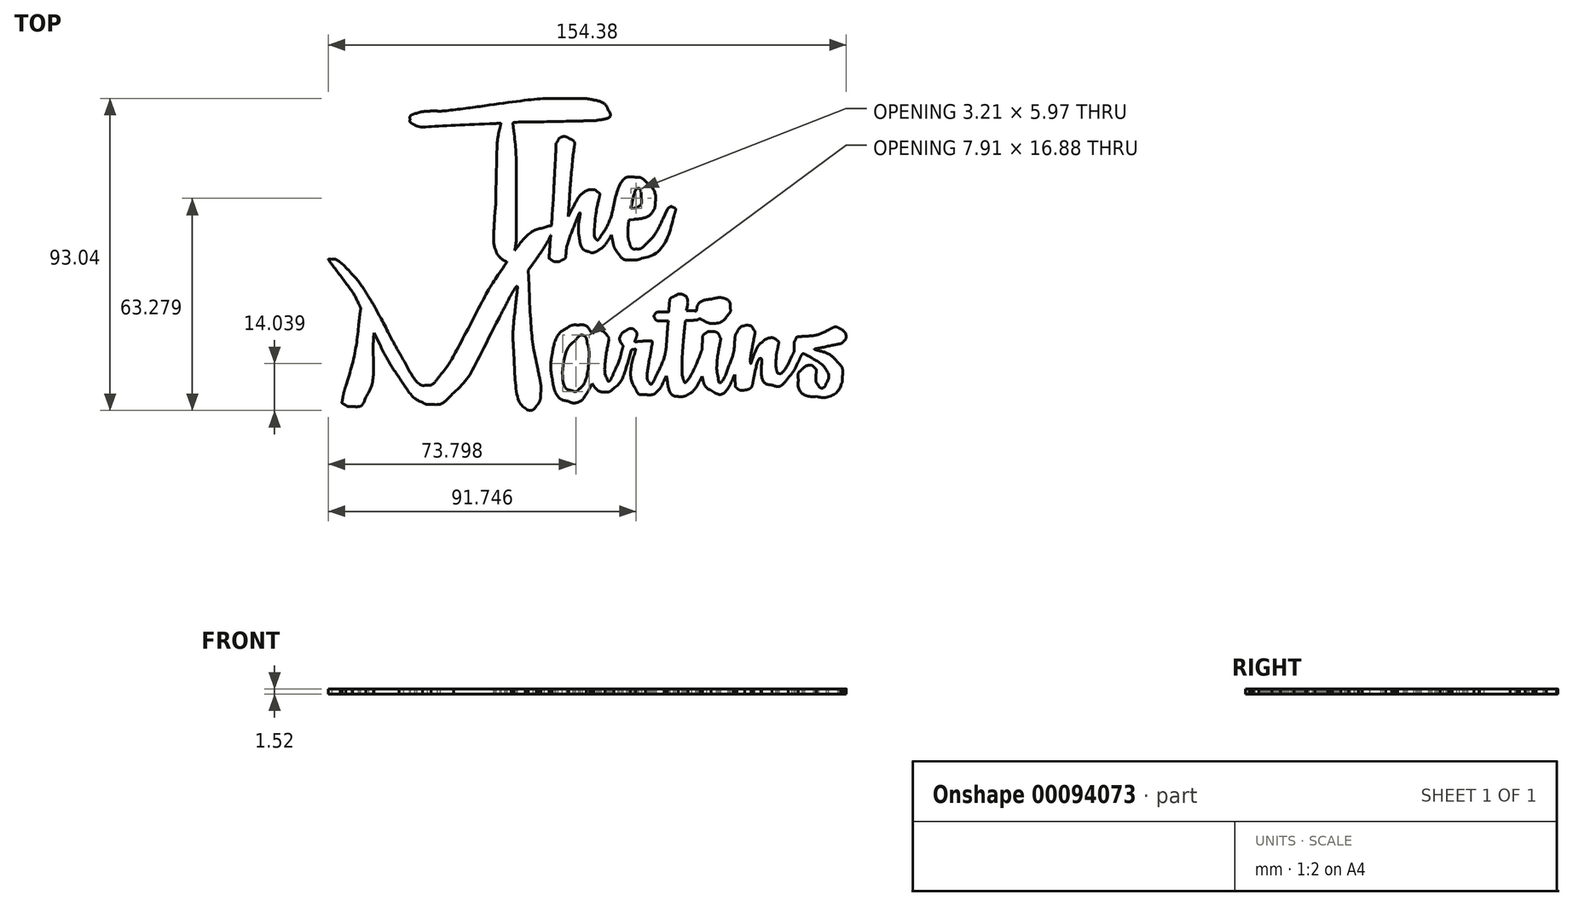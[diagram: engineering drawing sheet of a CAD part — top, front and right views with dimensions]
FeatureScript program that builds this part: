
annotation { "Feature Type Name" : "Feature", "Feature Type Description" : "" }
export const myFeature = defineFeature(function(context is Context, id is Id, definition is map)
    precondition{}
    {
        {
            var Q0;
            Q0=qCreatedBy(makeId("Top.planeOp"),FACE);
            var sketch = newSketch(context, id + "F0", { "sketchPlane" : qUnion([Q0])});
            skLineSegment(sketch, "E0", {"start": v(-54.49, 3450.18) * mm, "end": v(-56.26, 3453.65) * mm});
            skLineSegment(sketch, "E1", {"start": v(-56.26, 3453.65) * mm, "end": v(-56.34, 3452) * mm});
            skLineSegment(sketch, "E2", {"start": v(-56.34, 3452) * mm, "end": v(-54.49, 3450.18) * mm});
            skLineSegment(sketch, "E3", {"start": v(-8.87, 3474.22) * mm, "end": v(-10.27, 3472.28) * mm});
            skLineSegment(sketch, "E4", {"start": v(-10.27, 3472.28) * mm, "end": v(-10.04, 3467.72) * mm});
            skLineSegment(sketch, "E5", {"start": v(-10.04, 3467.72) * mm, "end": v(-8.87, 3474.22) * mm});
            skLineSegment(sketch, "E6", {"start": v(8.5, 3453.96) * mm, "end": v(8.88, 3453.46) * mm});
            skLineSegment(sketch, "E7", {"start": v(8.88, 3453.46) * mm, "end": v(9.39, 3453.76) * mm});
            skLineSegment(sketch, "E8", {"start": v(9.39, 3453.76) * mm, "end": v(8.5, 3453.96) * mm});
            skLineSegment(sketch, "E9", {"start": v(31.4, 3456.4) * mm, "end": v(31.5, 3457.23) * mm});
            skLineSegment(sketch, "E10", {"start": v(31.5, 3457.23) * mm, "end": v(30.1, 3457.23) * mm});
            skLineSegment(sketch, "E11", {"start": v(30.1, 3457.23) * mm, "end": v(31.4, 3456.4) * mm});
            skLineSegment(sketch, "E12", {"start": v(37.13, 3461.41) * mm, "end": v(36.9, 3460.24) * mm});
            skLineSegment(sketch, "E13", {"start": v(36.9, 3460.24) * mm, "end": v(38.12, 3460.24) * mm});
            skLineSegment(sketch, "E14", {"start": v(38.12, 3460.24) * mm, "end": v(37.13, 3461.41) * mm});
            skLineSegment(sketch, "E15", {"start": v(38.35, 3457.4) * mm, "end": v(36.61, 3457.31) * mm});
            skLineSegment(sketch, "E16", {"start": v(36.61, 3457.31) * mm, "end": v(36.43, 3455.5) * mm});
            skLineSegment(sketch, "E17", {"start": v(36.43, 3455.5) * mm, "end": v(38.35, 3457.4) * mm});
            skLineSegment(sketch, "E18", {"start": v(51.4, 3439.4) * mm, "end": v(51.32, 3441.18) * mm});
            skLineSegment(sketch, "E19", {"start": v(51.32, 3441.18) * mm, "end": v(50.86, 3440.31) * mm});
            skLineSegment(sketch, "E20", {"start": v(50.86, 3440.31) * mm, "end": v(51.4, 3439.4) * mm});
            skLineSegment(sketch, "E21", {"start": v(41.74, 3440.04) * mm, "end": v(41.56, 3440.76) * mm});
            skLineSegment(sketch, "E22", {"start": v(41.56, 3440.76) * mm, "end": v(41.03, 3439.73) * mm});
            skLineSegment(sketch, "E23", {"start": v(41.03, 3439.73) * mm, "end": v(41.74, 3440.04) * mm});
            skLineSegment(sketch, "E24", {"start": v(31.16, 3439.74) * mm, "end": v(30.96, 3440.82) * mm});
            skLineSegment(sketch, "E25", {"start": v(30.96, 3440.82) * mm, "end": v(30.45, 3439.87) * mm});
            skLineSegment(sketch, "E26", {"start": v(30.45, 3439.87) * mm, "end": v(31.16, 3439.74) * mm});
            skLineSegment(sketch, "E27", {"start": v(9.34, 3437.83) * mm, "end": v(8.78, 3438.57) * mm});
            skLineSegment(sketch, "E28", {"start": v(8.78, 3438.57) * mm, "end": v(8.19, 3437.35) * mm});
            skLineSegment(sketch, "E29", {"start": v(8.19, 3437.35) * mm, "end": v(9.34, 3437.83) * mm});
            skLineSegment(sketch, "E30", {"start": v(1.75, 3489.42) * mm, "end": v(1.66, 3488.4) * mm});
            skLineSegment(sketch, "E31", {"start": v(1.66, 3488.4) * mm, "end": v(2.42, 3489.81) * mm});
            skLineSegment(sketch, "E32", {"start": v(2.42, 3489.81) * mm, "end": v(1.75, 3489.42) * mm});
            skLineSegment(sketch, "E33", {"start": v(21.22, 3487.5) * mm, "end": v(19.72, 3487.31) * mm});
            skLineSegment(sketch, "E34", {"start": v(19.72, 3487.31) * mm, "end": v(19.6, 3485.98) * mm});
            skLineSegment(sketch, "E35", {"start": v(19.6, 3485.98) * mm, "end": v(21.22, 3487.5) * mm});
            skLineSegment(sketch, "E36", {"start": v(14.8, 3481.58) * mm, "end": v(14.54, 3482.83) * mm});
            skLineSegment(sketch, "E37", {"start": v(14.54, 3482.83) * mm, "end": v(14.13, 3482.13) * mm});
            skLineSegment(sketch, "E38", {"start": v(14.13, 3482.13) * mm, "end": v(14.8, 3481.58) * mm});
            skLineSegment(sketch, "E39", {"start": v(-3.19, 3475.34) * mm, "end": v(-3.19, 3475.34) * mm});
            skLineSegment(sketch, "E40", {"start": v(20.42, 3491.25) * mm, "end": v(20.3, 3490.8) * mm});
            skLineSegment(sketch, "E41", {"start": v(20.3, 3490.8) * mm, "end": v(21.22, 3490.9) * mm});
            skLineSegment(sketch, "E42", {"start": v(21.22, 3490.9) * mm, "end": v(20.42, 3491.25) * mm});
            skFitSpline(sketch, "E43", {"points": [v(-10.23, 3430.63) * mm, v(-10.43, 3430.66) * mm, v(-10.81, 3430.92) * mm, v(-11.1, 3431.2) * mm]});
            skFitSpline(sketch, "E44", {"points": [v(-11.1, 3431.2) * mm, v(-12.81, 3432.91) * mm, v(-14.07, 3438.99) * mm, v(-14.56, 3447.98) * mm]});
            skFitSpline(sketch, "E45", {"points": [v(-14.56, 3447.98) * mm, v(-14.79, 3452.08) * mm, v(-14.67, 3455.56) * mm, v(-14.17, 3460.4) * mm]});
            skFitSpline(sketch, "E46", {"points": [v(-14.17, 3460.4) * mm, v(-13.75, 3464.32) * mm, v(-13.52, 3467.51) * mm, v(-13.64, 3467.51) * mm]});
            skFitSpline(sketch, "E47", {"points": [v(-13.64, 3467.51) * mm, v(-13.72, 3467.51) * mm, v(-14.71, 3466.04) * mm, v(-15.38, 3464.91) * mm]});
            skFitSpline(sketch, "E48", {"points": [v(-15.38, 3464.91) * mm, v(-15.64, 3464.47) * mm, v(-17.24, 3461.4) * mm, v(-18.93, 3458.1) * mm]});
            skFitSpline(sketch, "E49", {"points": [v(-18.93, 3458.1) * mm, v(-26.38, 3443.57) * mm, v(-28.95, 3439.34) * mm, v(-32.5, 3435.8) * mm]});
            skFitSpline(sketch, "E50", {"points": [v(-32.5, 3435.8) * mm, v(-35.08, 3433.23) * mm, v(-36.76, 3432.36) * mm, v(-39.15, 3432.34) * mm]});
            skFitSpline(sketch, "E51", {"points": [v(-39.15, 3432.34) * mm, v(-40.51, 3432.33) * mm, v(-40.65, 3432.36) * mm, v(-41.78, 3432.93) * mm]});
            skFitSpline(sketch, "E52", {"points": [v(-41.78, 3432.93) * mm, v(-43.95, 3434.03) * mm, v(-45.66, 3435.87) * mm, v(-48.73, 3440.4) * mm]});
            skFitSpline(sketch, "E53", {"points": [v(-48.73, 3440.4) * mm, v(-50.96, 3443.68) * mm, v(-52.51, 3446.32) * mm, v(-54.49, 3450.18) * mm]});
            skFitSpline(sketch, "E54", {"points": [v(-56.34, 3452) * mm, v(-56.4, 3451.1) * mm, v(-56.43, 3448.86) * mm, v(-56.42, 3447.04) * mm]});
            skFitSpline(sketch, "E55", {"points": [v(-56.42, 3447.04) * mm, v(-56.4, 3441.12) * mm, v(-57, 3437.63) * mm, v(-58.57, 3434.48) * mm]});
            skFitSpline(sketch, "E56", {"points": [v(-58.57, 3434.48) * mm, v(-59.68, 3432.28) * mm, v(-60.52, 3431.7) * mm, v(-62.62, 3431.7) * mm]});
            skFitSpline(sketch, "E57", {"points": [v(-62.62, 3431.7) * mm, v(-63.74, 3431.7) * mm, v(-64.07, 3431.76) * mm, v(-64.62, 3432.07) * mm]});
            skFitSpline(sketch, "E58", {"points": [v(-64.62, 3432.07) * mm, v(-65.6, 3432.63) * mm, v(-65.7, 3432.94) * mm, v(-65.47, 3434.41) * mm]});
            skFitSpline(sketch, "E59", {"points": [v(-65.47, 3434.41) * mm, v(-65.36, 3435.09) * mm, v(-64.98, 3436.6) * mm, v(-64.63, 3437.78) * mm]});
            skFitSpline(sketch, "E60", {"points": [v(-64.63, 3437.78) * mm, v(-62.74, 3444.11) * mm, v(-61.4, 3450.5) * mm, v(-60.73, 3456.42) * mm]});
            skFitSpline(sketch, "E61", {"points": [v(-60.73, 3456.42) * mm, v(-60.56, 3457.87) * mm, v(-60.38, 3459.37) * mm, v(-60.33, 3459.77) * mm]});
            skFitSpline(sketch, "E62", {"points": [v(-60.33, 3459.77) * mm, v(-60.17, 3461.02) * mm, v(-60.2, 3461.18) * mm, v(-60.95, 3462.73) * mm]});
            skFitSpline(sketch, "E63", {"points": [v(-60.95, 3462.73) * mm, v(-61.92, 3464.74) * mm, v(-63.23, 3466.73) * mm, v(-66.27, 3470.77) * mm]});
            skFitSpline(sketch, "E64", {"points": [v(-66.27, 3470.77) * mm, v(-69.72, 3475.38) * mm, v(-69.82, 3475.58) * mm, v(-68.73, 3475.58) * mm]});
            skFitSpline(sketch, "E65", {"points": [v(-68.73, 3475.58) * mm, v(-67.74, 3475.58) * mm, v(-65.03, 3473.61) * mm, v(-63.01, 3471.44) * mm]});
            skFitSpline(sketch, "E66", {"points": [v(-63.01, 3471.44) * mm, v(-61.56, 3469.86) * mm, v(-59.31, 3466.84) * mm, v(-57.85, 3464.48) * mm]});
            skFitSpline(sketch, "E67", {"points": [v(-57.85, 3464.48) * mm, v(-56.4, 3462.14) * mm, v(-54.94, 3459.5) * mm, v(-51.63, 3453.21) * mm]});
            skFitSpline(sketch, "E68", {"points": [v(-51.63, 3453.21) * mm, v(-50.26, 3450.61) * mm, v(-48.98, 3448.23) * mm, v(-48.79, 3447.92) * mm]});
            skFitSpline(sketch, "E69", {"points": [v(-48.79, 3447.92) * mm, v(-48.59, 3447.6) * mm, v(-47.96, 3446.53) * mm, v(-47.4, 3445.52) * mm]});
            skFitSpline(sketch, "E70", {"points": [v(-47.4, 3445.52) * mm, v(-44.77, 3440.86) * mm, v(-42.17, 3438.12) * mm, v(-40.37, 3438.1) * mm]});
            skFitSpline(sketch, "E71", {"points": [v(-40.37, 3438.1) * mm, v(-39.2, 3438.1) * mm, v(-38.13, 3438.9) * mm, v(-36.5, 3441) * mm]});
            skFitSpline(sketch, "E72", {"points": [v(-36.5, 3441) * mm, v(-34.1, 3444.1) * mm, v(-32.06, 3447.55) * mm, v(-27.14, 3456.87) * mm]});
            skFitSpline(sketch, "E73", {"points": [v(-27.14, 3456.87) * mm, v(-22.54, 3465.6) * mm, v(-20.6, 3468.94) * mm, v(-17.3, 3473.68) * mm]});
            skFitSpline(sketch, "E74", {"points": [v(-17.3, 3473.68) * mm, v(-12.76, 3480.23) * mm, v(-8.86, 3484) * mm, v(-5.58, 3485) * mm]});
            skFitSpline(sketch, "E75", {"points": [v(-5.58, 3485) * mm, v(-3.72, 3485.56) * mm, v(-2.98, 3485.12) * mm, v(-3.3, 3483.65) * mm]});
            skFitSpline(sketch, "E76", {"points": [v(-3.3, 3483.65) * mm, v(-3.4, 3483.2) * mm, v(-3.66, 3482.48) * mm, v(-3.89, 3482.03) * mm]});
            skFitSpline(sketch, "E77", {"points": [v(-3.89, 3482.03) * mm, v(-4.58, 3480.66) * mm, v(-7.39, 3476.26) * mm, v(-8.87, 3474.22) * mm]});
            skFitSpline(sketch, "E78", {"points": [v(-10.04, 3467.72) * mm, v(-9.45, 3456.35) * mm, v(-8.8, 3450.07) * mm, v(-7.6, 3443.95) * mm]});
            skFitSpline(sketch, "E79", {"points": [v(-7.6, 3443.95) * mm, v(-6.62, 3439.05) * mm, v(-6.42, 3437.56) * mm, v(-6.5, 3435.7) * mm]});
            skFitSpline(sketch, "E80", {"points": [v(-6.5, 3435.7) * mm, v(-6.58, 3434.13) * mm, v(-6.98, 3432.94) * mm, v(-7.84, 3431.82) * mm]});
            skFitSpline(sketch, "E81", {"points": [v(-7.84, 3431.82) * mm, v(-8.49, 3430.97) * mm, v(-9.42, 3430.5) * mm, v(-10.23, 3430.63) * mm]});
            skFitSpline(sketch, "E82", {"points": [v(1.65, 3433.3) * mm, v(-0.63, 3433.99) * mm, v(-2.37, 3436.52) * mm, v(-3.08, 3440.16) * mm]});
            skFitSpline(sketch, "E83", {"points": [v(-3.08, 3440.16) * mm, v(-3.41, 3441.9) * mm, v(-3.42, 3445.47) * mm, v(-3.08, 3447.21) * mm]});
            skFitSpline(sketch, "E84", {"points": [v(-3.08, 3447.21) * mm, v(-2.4, 3450.82) * mm, v(-0.8, 3453.68) * mm, v(1.3, 3455.06) * mm]});
            skFitSpline(sketch, "E85", {"points": [v(1.3, 3455.06) * mm, v(2.44, 3455.8) * mm, v(3.15, 3456) * mm, v(4.6, 3456) * mm]});
            skFitSpline(sketch, "E86", {"points": [v(4.6, 3456) * mm, v(6.4, 3456) * mm, v(7.3, 3455.52) * mm, v(8.5, 3453.96) * mm]});
            skFitSpline(sketch, "E87", {"points": [v(9.39, 3453.76) * mm, v(10.43, 3454.4) * mm, v(12.3, 3454.01) * mm, v(13.18, 3452.98) * mm]});
            skFitSpline(sketch, "E88", {"points": [v(13.18, 3452.98) * mm, v(13.78, 3452.26) * mm, v(13.83, 3451.9) * mm, v(13.55, 3450.32) * mm]});
            skFitSpline(sketch, "E89", {"points": [v(13.55, 3450.32) * mm, v(12.85, 3446.4) * mm, v(12.66, 3441.4) * mm, v(13.16, 3440.28) * mm]});
            skFitSpline(sketch, "E90", {"points": [v(13.16, 3440.28) * mm, v(13.65, 3439.2) * mm, v(14.22, 3439.61) * mm, v(15.28, 3441.82) * mm]});
            skFitSpline(sketch, "E91", {"points": [v(15.28, 3441.82) * mm, v(16.01, 3443.36) * mm, v(17.3, 3446.76) * mm, v(17.47, 3447.61) * mm]});
            skFitSpline(sketch, "E92", {"points": [v(17.47, 3447.61) * mm, v(17.53, 3447.9) * mm, v(17.69, 3448.49) * mm, v(17.82, 3448.91) * mm]});
            skFitSpline(sketch, "E93", {"points": [v(17.82, 3448.91) * mm, v(18.06, 3449.65) * mm, v(18.05, 3449.7) * mm, v(17.72, 3450.31) * mm]});
            skFitSpline(sketch, "E94", {"points": [v(17.72, 3450.31) * mm, v(17, 3451.57) * mm, v(17.58, 3453.4) * mm, v(18.97, 3454.35) * mm]});
            skFitSpline(sketch, "E95", {"points": [v(18.97, 3454.35) * mm, v(19.74, 3454.87) * mm, v(21.06, 3454.85) * mm, v(21.6, 3454.32) * mm]});
            skFitSpline(sketch, "E96", {"points": [v(21.6, 3454.32) * mm, v(22.05, 3453.86) * mm, v(22.11, 3452.81) * mm, v(21.74, 3451.78) * mm]});
            skFitSpline(sketch, "E97", {"points": [v(21.74, 3451.78) * mm, v(21.62, 3451.43) * mm, v(21.51, 3451.12) * mm, v(21.51, 3451.08) * mm]});
            skFitSpline(sketch, "E98", {"points": [v(21.51, 3451.08) * mm, v(21.51, 3451.05) * mm, v(22.37, 3451.07) * mm, v(23.41, 3451.13) * mm]});
            skFitSpline(sketch, "E99", {"points": [v(23.41, 3451.13) * mm, v(26.28, 3451.3) * mm, v(26.73, 3451.06) * mm, v(26.53, 3449.44) * mm]});
            skFitSpline(sketch, "E100", {"points": [v(26.53, 3449.44) * mm, v(26.48, 3449.07) * mm, v(26.25, 3447.74) * mm, v(26.02, 3446.48) * mm]});
            skFitSpline(sketch, "E101", {"points": [v(26.02, 3446.48) * mm, v(25.46, 3443.48) * mm, v(25.3, 3439.73) * mm, v(25.68, 3439.13) * mm]});
            skFitSpline(sketch, "E102", {"points": [v(25.68, 3439.13) * mm, v(26.22, 3438.3) * mm, v(26.83, 3438.77) * mm, v(27.84, 3440.79) * mm]});
            skFitSpline(sketch, "E103", {"points": [v(27.84, 3440.79) * mm, v(28.98, 3443.07) * mm, v(30.32, 3446.5) * mm, v(30.65, 3447.98) * mm]});
            skFitSpline(sketch, "E104", {"points": [v(30.65, 3447.98) * mm, v(30.75, 3448.42) * mm, v(30.94, 3450.3) * mm, v(31.07, 3452.17) * mm]});
            skFitSpline(sketch, "E105", {"points": [v(31.07, 3452.17) * mm, v(31.2, 3454.04) * mm, v(31.36, 3455.95) * mm, v(31.4, 3456.4) * mm]});
            skFitSpline(sketch, "E106", {"points": [v(30.1, 3457.23) * mm, v(28.51, 3457.23) * mm, v(27.74, 3457.52) * mm, v(27.39, 3458.25) * mm]});
            skFitSpline(sketch, "E107", {"points": [v(27.39, 3458.25) * mm, v(27.2, 3458.62) * mm, v(27.21, 3458.73) * mm, v(27.44, 3459.08) * mm]});
            skFitSpline(sketch, "E108", {"points": [v(27.44, 3459.08) * mm, v(27.84, 3459.7) * mm, v(28.6, 3459.92) * mm, v(30.2, 3459.92) * mm]});
            skFitSpline(sketch, "E109", {"points": [v(30.2, 3459.92) * mm, v(31.24, 3459.92) * mm, v(31.63, 3459.98) * mm, v(31.63, 3460.12) * mm]});
            skFitSpline(sketch, "E110", {"points": [v(31.63, 3460.12) * mm, v(31.64, 3460.23) * mm, v(31.7, 3460.98) * mm, v(31.78, 3461.78) * mm]});
            skFitSpline(sketch, "E111", {"points": [v(31.78, 3461.78) * mm, v(31.95, 3463.48) * mm, v(32.26, 3464.06) * mm, v(33.28, 3464.52) * mm]});
            skFitSpline(sketch, "E112", {"points": [v(33.28, 3464.52) * mm, v(34.85, 3465.24) * mm, v(36.9, 3464.44) * mm, v(37.27, 3462.97) * mm]});
            skFitSpline(sketch, "E113", {"points": [v(37.27, 3462.97) * mm, v(37.32, 3462.76) * mm, v(37.26, 3462.06) * mm, v(37.13, 3461.41) * mm]});
            skFitSpline(sketch, "E114", {"points": [v(38.12, 3460.24) * mm, v(38.8, 3460.24) * mm, v(39.46, 3460.2) * mm, v(39.58, 3460.15) * mm]});
            skFitSpline(sketch, "E115", {"points": [v(39.58, 3460.15) * mm, v(39.75, 3460.09) * mm, v(39.86, 3460.25) * mm, v(39.98, 3460.74) * mm]});
            skFitSpline(sketch, "E116", {"points": [v(39.98, 3460.74) * mm, v(40.34, 3462.16) * mm, v(42.17, 3463.38) * mm, v(44.43, 3463.73) * mm]});
            skFitSpline(sketch, "E117", {"points": [v(44.43, 3463.73) * mm, v(47.26, 3464.16) * mm, v(49.63, 3463.1) * mm, v(49.9, 3461.25) * mm]});
            skFitSpline(sketch, "E118", {"points": [v(49.9, 3461.25) * mm, v(50.05, 3460.28) * mm, v(49.87, 3459.72) * mm, v(49.16, 3458.9) * mm]});
            skFitSpline(sketch, "E119", {"points": [v(49.16, 3458.9) * mm, v(47.58, 3457.1) * mm, v(44.1, 3456.49) * mm, v(41.6, 3457.56) * mm]});
            skFitSpline(sketch, "E120", {"points": [v(41.6, 3457.56) * mm, v(40.93, 3457.85) * mm, v(40.78, 3457.87) * mm, v(40.46, 3457.68) * mm]});
            skFitSpline(sketch, "E121", {"points": [v(40.46, 3457.68) * mm, v(40.24, 3457.56) * mm, v(39.37, 3457.44) * mm, v(38.35, 3457.4) * mm]});
            skFitSpline(sketch, "E122", {"points": [v(36.43, 3455.5) * mm, v(35.85, 3449.64) * mm, v(35.63, 3441.23) * mm, v(36.03, 3439.87) * mm]});
            skFitSpline(sketch, "E123", {"points": [v(36.03, 3439.87) * mm, v(36.3, 3438.95) * mm, v(36.63, 3438.86) * mm, v(37.2, 3439.54) * mm]});
            skFitSpline(sketch, "E124", {"points": [v(37.2, 3439.54) * mm, v(37.77, 3440.2) * mm, v(39.92, 3444.54) * mm, v(40.85, 3446.88) * mm]});
            skFitSpline(sketch, "E125", {"points": [v(40.85, 3446.88) * mm, v(41.5, 3448.49) * mm, v(41.55, 3448.76) * mm, v(41.64, 3450.48) * mm]});
            skFitSpline(sketch, "E126", {"points": [v(41.64, 3450.48) * mm, v(41.74, 3452.57) * mm, v(41.94, 3453.1) * mm, v(42.87, 3453.73) * mm]});
            skFitSpline(sketch, "E127", {"points": [v(42.87, 3453.73) * mm, v(43.33, 3454.04) * mm, v(43.56, 3454.1) * mm, v(44.38, 3454.04) * mm]});
            skFitSpline(sketch, "E128", {"points": [v(44.38, 3454.04) * mm, v(45.58, 3453.97) * mm, v(46.36, 3453.48) * mm, v(46.82, 3452.54) * mm]});
            skFitSpline(sketch, "E129", {"points": [v(46.82, 3452.54) * mm, v(47.14, 3451.9) * mm, v(47.14, 3451.83) * mm, v(46.9, 3450.56) * mm]});
            skFitSpline(sketch, "E130", {"points": [v(46.9, 3450.56) * mm, v(46.27, 3447.14) * mm, v(45.98, 3442.24) * mm, v(46.33, 3440.73) * mm]});
            skFitSpline(sketch, "E131", {"points": [v(46.33, 3440.73) * mm, v(46.79, 3438.75) * mm, v(47.88, 3439.7) * mm, v(49.3, 3443.32) * mm]});
            skFitSpline(sketch, "E132", {"points": [v(49.3, 3443.32) * mm, v(50.58, 3446.53) * mm, v(51.04, 3448.24) * mm, v(51.23, 3450.39) * mm]});
            skFitSpline(sketch, "E133", {"points": [v(51.23, 3450.39) * mm, v(51.42, 3452.59) * mm, v(51.57, 3453.25) * mm, v(52.06, 3453.95) * mm]});
            skFitSpline(sketch, "E134", {"points": [v(52.06, 3453.95) * mm, v(53.08, 3455.4) * mm, v(55.99, 3455.79) * mm, v(56.93, 3454.6) * mm]});
            skFitSpline(sketch, "E135", {"points": [v(56.93, 3454.6) * mm, v(57.35, 3454.06) * mm, v(57.33, 3453.62) * mm, v(56.79, 3450.73) * mm]});
            skFitSpline(sketch, "E136", {"points": [v(56.79, 3450.73) * mm, v(56.25, 3447.85) * mm, v(55.93, 3445.48) * mm, v(56, 3444.82) * mm]});
            skFitSpline(sketch, "E137", {"points": [v(56, 3444.82) * mm, v(56.05, 3444.42) * mm, v(56.13, 3444.54) * mm, v(56.52, 3445.61) * mm]});
            skFitSpline(sketch, "E138", {"points": [v(56.52, 3445.61) * mm, v(57.38, 3448.02) * mm, v(58.6, 3450.16) * mm, v(59.53, 3450.9) * mm]});
            skFitSpline(sketch, "E139", {"points": [v(59.53, 3450.9) * mm, v(60.77, 3451.89) * mm, v(62.9, 3452.15) * mm, v(63.86, 3451.43) * mm]});
            skFitSpline(sketch, "E140", {"points": [v(63.86, 3451.43) * mm, v(64.36, 3451.05) * mm, v(64.39, 3450.58) * mm, v(64, 3448.62) * mm]});
            skFitSpline(sketch, "E141", {"points": [v(64, 3448.62) * mm, v(63.7, 3447.15) * mm, v(63.64, 3443.1) * mm, v(63.9, 3442.17) * mm]});
            skFitSpline(sketch, "E142", {"points": [v(63.9, 3442.17) * mm, v(64.03, 3441.7) * mm, v(64.14, 3441.58) * mm, v(64.44, 3441.58) * mm]});
            skFitSpline(sketch, "E143", {"points": [v(64.44, 3441.58) * mm, v(65.16, 3441.58) * mm, v(66.94, 3443.92) * mm, v(68.29, 3446.64) * mm]});
            skFitSpline(sketch, "E144", {"points": [v(68.29, 3446.64) * mm, v(69, 3448.1) * mm, v(69.03, 3448.18) * mm, v(69, 3449.46) * mm]});
            skFitSpline(sketch, "E145", {"points": [v(69, 3449.46) * mm, v(68.96, 3450.51) * mm, v(69.02, 3450.9) * mm, v(69.27, 3451.4) * mm]});
            skFitSpline(sketch, "E146", {"points": [v(69.27, 3451.4) * mm, v(69.74, 3452.32) * mm, v(70.12, 3452.49) * mm, v(72.08, 3452.65) * mm]});
            skFitSpline(sketch, "E147", {"points": [v(72.08, 3452.65) * mm, v(74.88, 3452.87) * mm, v(77.19, 3453.52) * mm, v(79.66, 3454.76) * mm]});
            skFitSpline(sketch, "E148", {"points": [v(79.66, 3454.76) * mm, v(80.98, 3455.43) * mm, v(81.6, 3455.48) * mm, v(82.42, 3454.98) * mm]});
            skFitSpline(sketch, "E149", {"points": [v(82.42, 3454.98) * mm, v(83.9, 3454.1) * mm, v(84.53, 3452.16) * mm, v(83.67, 3451.16) * mm]});
            skFitSpline(sketch, "E150", {"points": [v(83.67, 3451.16) * mm, v(83.2, 3450.62) * mm, v(82, 3450.27) * mm, v(77.34, 3449.32) * mm]});
            skFitSpline(sketch, "E151", {"points": [v(77.34, 3449.32) * mm, v(76.09, 3449.06) * mm, v(75.04, 3448.83) * mm, v(75.02, 3448.8) * mm]});
            skFitSpline(sketch, "E152", {"points": [v(75.02, 3448.8) * mm, v(74.99, 3448.78) * mm, v(75.52, 3448.6) * mm, v(76.18, 3448.4) * mm]});
            skFitSpline(sketch, "E153", {"points": [v(76.18, 3448.4) * mm, v(78.52, 3447.71) * mm, v(80.46, 3446.54) * mm, v(81.93, 3444.94) * mm]});
            skFitSpline(sketch, "E154", {"points": [v(81.93, 3444.94) * mm, v(83.18, 3443.56) * mm, v(83.4, 3442.95) * mm, v(83.41, 3440.87) * mm]});
            skFitSpline(sketch, "E155", {"points": [v(83.41, 3440.87) * mm, v(83.42, 3439.33) * mm, v(83.37, 3439.04) * mm, v(83.03, 3438.37) * mm]});
            skFitSpline(sketch, "E156", {"points": [v(83.03, 3438.37) * mm, v(81.86, 3436.07) * mm, v(78.56, 3434.44) * mm, v(75.62, 3434.7) * mm]});
            skFitSpline(sketch, "E157", {"points": [v(75.62, 3434.7) * mm, v(72.47, 3434.97) * mm, v(70.43, 3436.9) * mm, v(70.25, 3439.75) * mm]});
            skFitSpline(sketch, "E158", {"points": [v(70.25, 3439.75) * mm, v(70.15, 3441.24) * mm, v(70.38, 3441.9) * mm, v(71.25, 3442.66) * mm]});
            skFitSpline(sketch, "E159", {"points": [v(71.25, 3442.66) * mm, v(72.45, 3443.72) * mm, v(74.35, 3443.95) * mm, v(75.22, 3443.14) * mm]});
            skFitSpline(sketch, "E160", {"points": [v(75.22, 3443.14) * mm, v(75.62, 3442.78) * mm, v(75.62, 3442.72) * mm, v(75.53, 3441.34) * mm]});
            skFitSpline(sketch, "E161", {"points": [v(75.53, 3441.34) * mm, v(75.42, 3439.73) * mm, v(75.59, 3438.91) * mm, v(76.17, 3438.14) * mm]});
            skFitSpline(sketch, "E162", {"points": [v(76.17, 3438.14) * mm, v(76.84, 3437.26) * mm, v(78.06, 3437.53) * mm, v(78.53, 3438.67) * mm]});
            skFitSpline(sketch, "E163", {"points": [v(78.53, 3438.67) * mm, v(79.34, 3440.6) * mm, v(77.6, 3443.93) * mm, v(74.77, 3445.83) * mm]});
            skFitSpline(sketch, "E164", {"points": [v(74.77, 3445.83) * mm, v(73.96, 3446.37) * mm, v(71.83, 3447.43) * mm, v(71.56, 3447.43) * mm]});
            skFitSpline(sketch, "E165", {"points": [v(71.56, 3447.43) * mm, v(71.47, 3447.42) * mm, v(70.93, 3446.44) * mm, v(70.35, 3445.25) * mm]});
            skFitSpline(sketch, "E166", {"points": [v(70.35, 3445.25) * mm, v(69.18, 3442.85) * mm, v(68.5, 3441.78) * mm, v(67.21, 3440.24) * mm]});
            skFitSpline(sketch, "E167", {"points": [v(67.21, 3440.24) * mm, v(65.55, 3438.27) * mm, v(64.24, 3437.68) * mm, v(62.46, 3438.1) * mm]});
            skFitSpline(sketch, "E168", {"points": [v(62.46, 3438.1) * mm, v(60.37, 3438.6) * mm, v(59.31, 3440.72) * mm, v(59.3, 3444.39) * mm]});
            skFitSpline(sketch, "E169", {"points": [v(59.3, 3444.39) * mm, v(59.3, 3445.38) * mm, v(59.24, 3446) * mm, v(59.14, 3446) * mm]});
            skFitSpline(sketch, "E170", {"points": [v(59.14, 3446) * mm, v(58.64, 3446) * mm, v(57.5, 3442.81) * mm, v(56.87, 3439.7) * mm]});
            skFitSpline(sketch, "E171", {"points": [v(56.87, 3439.7) * mm, v(56.66, 3438.64) * mm, v(56.4, 3437.67) * mm, v(56.29, 3437.53) * mm]});
            skFitSpline(sketch, "E172", {"points": [v(56.29, 3437.53) * mm, v(55.99, 3437.17) * mm, v(55.05, 3436.73) * mm, v(54.3, 3436.6) * mm]});
            skFitSpline(sketch, "E173", {"points": [v(54.3, 3436.6) * mm, v(53.49, 3436.47) * mm, v(52.49, 3436.73) * mm, v(51.91, 3437.22) * mm]});
            skFitSpline(sketch, "E174", {"points": [v(51.91, 3437.22) * mm, v(51.5, 3437.58) * mm, v(51.47, 3437.67) * mm, v(51.4, 3439.4) * mm]});
            skFitSpline(sketch, "E175", {"points": [v(50.86, 3440.31) * mm, v(48.84, 3436.47) * mm, v(46.8, 3435.29) * mm, v(44.3, 3436.53) * mm]});
            skFitSpline(sketch, "E176", {"points": [v(44.3, 3436.53) * mm, v(43.01, 3437.18) * mm, v(42.18, 3438.33) * mm, v(41.74, 3440.04) * mm]});
            skFitSpline(sketch, "E177", {"points": [v(41.03, 3439.73) * mm, v(40.02, 3437.8) * mm, v(38.51, 3436) * mm, v(37.32, 3435.3) * mm]});
            skFitSpline(sketch, "E178", {"points": [v(37.32, 3435.3) * mm, v(36.62, 3434.88) * mm, v(35.1, 3434.57) * mm, v(34.43, 3434.7) * mm]});
            skFitSpline(sketch, "E179", {"points": [v(34.43, 3434.7) * mm, v(32.81, 3435.04) * mm, v(31.73, 3436.7) * mm, v(31.16, 3439.74) * mm]});
            skFitSpline(sketch, "E180", {"points": [v(30.45, 3439.87) * mm, v(28.85, 3436.88) * mm, v(26.84, 3435.26) * mm, v(24.72, 3435.26) * mm]});
            skFitSpline(sketch, "E181", {"points": [v(24.72, 3435.26) * mm, v(23.12, 3435.25) * mm, v(22.42, 3435.67) * mm, v(21.73, 3437.03) * mm]});
            skFitSpline(sketch, "E182", {"points": [v(21.73, 3437.03) * mm, v(20.52, 3439.4) * mm, v(20.43, 3443.45) * mm, v(21.5, 3447.61) * mm]});
            skFitSpline(sketch, "E183", {"points": [v(21.5, 3447.61) * mm, v(21.66, 3448.25) * mm, v(21.78, 3448.79) * mm, v(21.77, 3448.8) * mm]});
            skFitSpline(sketch, "E184", {"points": [v(21.77, 3448.8) * mm, v(21.76, 3448.81) * mm, v(21.47, 3448.77) * mm, v(21.13, 3448.72) * mm]});
            skFitSpline(sketch, "E185", {"points": [v(21.13, 3448.72) * mm, v(20.65, 3448.64) * mm, v(20.48, 3448.53) * mm, v(20.4, 3448.22) * mm]});
            skFitSpline(sketch, "E186", {"points": [v(20.4, 3448.22) * mm, v(18.5, 3441.82) * mm, v(17.13, 3438.88) * mm, v(15.28, 3437.18) * mm]});
            skFitSpline(sketch, "E187", {"points": [v(15.28, 3437.18) * mm, v(14.36, 3436.34) * mm, v(13.69, 3436.05) * mm, v(12.67, 3436.05) * mm]});
            skFitSpline(sketch, "E188", {"points": [v(12.67, 3436.05) * mm, v(11.56, 3436.05) * mm, v(10.06, 3436.84) * mm, v(9.34, 3437.83) * mm]});
            skFitSpline(sketch, "E189", {"points": [v(8.19, 3437.35) * mm, v(7.86, 3436.67) * mm, v(7.32, 3435.77) * mm, v(7, 3435.33) * mm]});
            skFitSpline(sketch, "E190", {"points": [v(7, 3435.33) * mm, v(5.68, 3433.58) * mm, v(3.47, 3432.74) * mm, v(1.65, 3433.3) * mm]});
            skFitSpline(sketch, "E191", {"points": [v(4.87, 3436.88) * mm, v(6.2, 3438.16) * mm, v(7.5, 3442.18) * mm, v(7.82, 3446) * mm]});
            skFitSpline(sketch, "E192", {"points": [v(7.82, 3446) * mm, v(7.93, 3447.24) * mm, v(7.71, 3449.27) * mm, v(7.34, 3450.53) * mm]});
            skFitSpline(sketch, "E193", {"points": [v(7.34, 3450.53) * mm, v(6.75, 3452.6) * mm, v(5.25, 3452.93) * mm, v(3.84, 3451.33) * mm]});
            skFitSpline(sketch, "E194", {"points": [v(3.84, 3451.33) * mm, v(1.17, 3448.28) * mm, v(0.55, 3437.8) * mm, v(2.97, 3436.44) * mm]});
            skFitSpline(sketch, "E195", {"points": [v(2.97, 3436.44) * mm, v(3.57, 3436.11) * mm, v(4.24, 3436.27) * mm, v(4.87, 3436.88) * mm]});
            skFitSpline(sketch, "E196", {"points": [v(-17.01, 3475.03) * mm, v(-18.06, 3475.58) * mm, v(-19.45, 3477.11) * mm, v(-19.83, 3478.13) * mm]});
            skFitSpline(sketch, "E197", {"points": [v(-19.83, 3478.13) * mm, v(-20.35, 3479.5) * mm, v(-20.53, 3482.84) * mm, v(-20.31, 3486.89) * mm]});
            skFitSpline(sketch, "E198", {"points": [v(-20.31, 3486.89) * mm, v(-20.22, 3488.67) * mm, v(-20.1, 3490.24) * mm, v(-20.06, 3490.37) * mm]});
            skFitSpline(sketch, "E199", {"points": [v(-20.06, 3490.37) * mm, v(-20.01, 3490.5) * mm, v(-19.91, 3493.56) * mm, v(-19.83, 3497.17) * mm]});
            skFitSpline(sketch, "E200", {"points": [v(-19.83, 3497.17) * mm, v(-19.6, 3507.22) * mm, v(-19.31, 3511.76) * mm, v(-18.72, 3514.48) * mm]});
            skFitSpline(sketch, "E201", {"points": [v(-18.72, 3514.48) * mm, v(-18.55, 3515.25) * mm, v(-18.42, 3515.95) * mm, v(-18.42, 3516.02) * mm]});
            skFitSpline(sketch, "E202", {"points": [v(-18.42, 3516.02) * mm, v(-18.42, 3516.1) * mm, v(-19.25, 3516.11) * mm, v(-20.27, 3516.07) * mm]});
            skFitSpline(sketch, "E203", {"points": [v(-20.27, 3516.07) * mm, v(-37.54, 3515.25) * mm, v(-43.16, 3515.18) * mm, v(-44.2, 3515.73) * mm]});
            skFitSpline(sketch, "E204", {"points": [v(-44.2, 3515.73) * mm, v(-45.16, 3516.24) * mm, v(-45.46, 3516.61) * mm, v(-45.46, 3517.3) * mm]});
            skFitSpline(sketch, "E205", {"points": [v(-45.46, 3517.3) * mm, v(-45.46, 3518.15) * mm, v(-44.86, 3518.71) * mm, v(-43.48, 3519.14) * mm]});
            skFitSpline(sketch, "E206", {"points": [v(-43.48, 3519.14) * mm, v(-42.35, 3519.49) * mm, v(-39.65, 3519.77) * mm, v(-37.46, 3519.78) * mm]});
            skFitSpline(sketch, "E207", {"points": [v(-37.46, 3519.78) * mm, v(-36.03, 3519.78) * mm, v(-30.17, 3520.43) * mm, v(-23.24, 3521.36) * mm]});
            skFitSpline(sketch, "E208", {"points": [v(-23.24, 3521.36) * mm, v(-10.96, 3523) * mm, v(-5.13, 3523.5) * mm, v(2.06, 3523.5) * mm]});
            skFitSpline(sketch, "E209", {"points": [v(2.06, 3523.5) * mm, v(6.51, 3523.5) * mm, v(7.48, 3523.45) * mm, v(8.62, 3523.2) * mm]});
            skFitSpline(sketch, "E210", {"points": [v(8.62, 3523.2) * mm, v(11.04, 3522.69) * mm, v(12.93, 3521.53) * mm, v(13.55, 3520.18) * mm]});
            skFitSpline(sketch, "E211", {"points": [v(13.55, 3520.18) * mm, v(14.3, 3518.5) * mm, v(13.61, 3517.7) * mm, v(10.93, 3517.15) * mm]});
            skFitSpline(sketch, "E212", {"points": [v(10.93, 3517.15) * mm, v(10.13, 3517) * mm, v(7.74, 3516.88) * mm, v(2.54, 3516.78) * mm]});
            skFitSpline(sketch, "E213", {"points": [v(2.54, 3516.78) * mm, v(-6.76, 3516.58) * mm, v(-14.63, 3516.34) * mm, v(-14.73, 3516.24) * mm]});
            skFitSpline(sketch, "E214", {"points": [v(-14.73, 3516.24) * mm, v(-14.77, 3516.2) * mm, v(-14.7, 3515.11) * mm, v(-14.56, 3513.82) * mm]});
            skFitSpline(sketch, "E215", {"points": [v(-14.56, 3513.82) * mm, v(-13.99, 3508.45) * mm, v(-13.78, 3502.87) * mm, v(-13.76, 3492.74) * mm]});
            skFitSpline(sketch, "E216", {"points": [v(-13.76, 3492.74) * mm, v(-13.75, 3482.67) * mm, v(-13.83, 3480.7) * mm, v(-14.4, 3477.64) * mm]});
            skFitSpline(sketch, "E217", {"points": [v(-14.4, 3477.64) * mm, v(-14.54, 3476.94) * mm, v(-14.81, 3476) * mm, v(-15.02, 3475.54) * mm]});
            skFitSpline(sketch, "E218", {"points": [v(-15.02, 3475.54) * mm, v(-15.36, 3474.78) * mm, v(-15.44, 3474.71) * mm, v(-15.92, 3474.72) * mm]});
            skFitSpline(sketch, "E219", {"points": [v(-15.92, 3474.72) * mm, v(-16.2, 3474.72) * mm, v(-16.7, 3474.86) * mm, v(-17.01, 3475.03) * mm]});
            skFitSpline(sketch, "E220", {"points": [v(-3.19, 3475.34) * mm, v(-4.06, 3475.87) * mm, v(-4.07, 3475.9) * mm, v(-3.72, 3480.44) * mm]});
            skFitSpline(sketch, "E221", {"points": [v(-3.72, 3480.44) * mm, v(-3.24, 3486.74) * mm, v(-2.64, 3496.05) * mm, v(-2.37, 3501.52) * mm]});
            skFitSpline(sketch, "E222", {"points": [v(-2.37, 3501.52) * mm, v(-1.94, 3509.93) * mm, v(-1.92, 3510.17) * mm, v(-1.5, 3510.76) * mm]});
            skFitSpline(sketch, "E223", {"points": [v(-1.5, 3510.76) * mm, v(-0.74, 3511.82) * mm, v(0.88, 3512.16) * mm, v(2.15, 3511.52) * mm]});
            skFitSpline(sketch, "E224", {"points": [v(2.15, 3511.52) * mm, v(3.15, 3511.01) * mm, v(3.62, 3510.26) * mm, v(3.5, 3509.34) * mm]});
            skFitSpline(sketch, "E225", {"points": [v(3.5, 3509.34) * mm, v(3.06, 3505.85) * mm, v(2.39, 3498.6) * mm, v(2.07, 3493.93) * mm]});
            skFitSpline(sketch, "E226", {"points": [v(2.07, 3493.93) * mm, v(1.94, 3492.01) * mm, v(1.8, 3489.98) * mm, v(1.75, 3489.42) * mm]});
            skFitSpline(sketch, "E227", {"points": [v(2.42, 3489.81) * mm, v(4.14, 3493.02) * mm, v(5.2, 3494.65) * mm, v(5.94, 3495.2) * mm]});
            skFitSpline(sketch, "E228", {"points": [v(5.94, 3495.2) * mm, v(7.15, 3496.08) * mm, v(9.57, 3496.32) * mm, v(10.48, 3495.64) * mm]});
            skFitSpline(sketch, "E229", {"points": [v(10.48, 3495.64) * mm, v(11.03, 3495.24) * mm, v(11.08, 3494.78) * mm, v(10.77, 3493.33) * mm]});
            skFitSpline(sketch, "E230", {"points": [v(10.77, 3493.33) * mm, v(10.07, 3490.13) * mm, v(9.6, 3482.03) * mm, v(10.07, 3481.55) * mm]});
            skFitSpline(sketch, "E231", {"points": [v(10.07, 3481.55) * mm, v(10.37, 3481.25) * mm, v(10.8, 3481.6) * mm, v(11.54, 3482.75) * mm]});
            skFitSpline(sketch, "E232", {"points": [v(11.54, 3482.75) * mm, v(13.07, 3485.13) * mm, v(14.39, 3488.2) * mm, v(15.18, 3491.24) * mm]});
            skFitSpline(sketch, "E233", {"points": [v(15.18, 3491.24) * mm, v(16.64, 3496.83) * mm, v(18.99, 3500) * mm, v(21.68, 3500.01) * mm]});
            skFitSpline(sketch, "E234", {"points": [v(21.68, 3500.01) * mm, v(22.95, 3500.02) * mm, v(23.87, 3499.61) * mm, v(25, 3498.55) * mm]});
            skFitSpline(sketch, "E235", {"points": [v(25, 3498.55) * mm, v(26.76, 3496.91) * mm, v(27.69, 3494.58) * mm, v(27.58, 3492.11) * mm]});
            skFitSpline(sketch, "E236", {"points": [v(27.58, 3492.11) * mm, v(27.53, 3491.1) * mm, v(27.45, 3490.79) * mm, v(27.08, 3490.24) * mm]});
            skFitSpline(sketch, "E237", {"points": [v(27.08, 3490.24) * mm, v(26.2, 3488.9) * mm, v(24, 3487.87) * mm, v(21.22, 3487.5) * mm]});
            skFitSpline(sketch, "E238", {"points": [v(19.6, 3485.98) * mm, v(19.45, 3484.15) * mm, v(19.6, 3481.61) * mm, v(19.93, 3480.57) * mm]});
            skFitSpline(sketch, "E239", {"points": [v(19.93, 3480.57) * mm, v(20.3, 3479.36) * mm, v(21.03, 3478.67) * mm, v(21.92, 3478.67) * mm]});
            skFitSpline(sketch, "E240", {"points": [v(21.92, 3478.67) * mm, v(22.93, 3478.67) * mm, v(23.9, 3479.22) * mm, v(25.25, 3480.55) * mm]});
            skFitSpline(sketch, "E241", {"points": [v(25.25, 3480.55) * mm, v(26.78, 3482.08) * mm, v(28.43, 3484.59) * mm, v(29.84, 3487.52) * mm]});
            skFitSpline(sketch, "E242", {"points": [v(29.84, 3487.52) * mm, v(30.45, 3488.78) * mm, v(31.06, 3490.06) * mm, v(31.21, 3490.37) * mm]});
            skFitSpline(sketch, "E243", {"points": [v(31.21, 3490.37) * mm, v(31.36, 3490.67) * mm, v(31.68, 3491.02) * mm, v(31.93, 3491.14) * mm]});
            skFitSpline(sketch, "E244", {"points": [v(31.93, 3491.14) * mm, v(32.33, 3491.33) * mm, v(32.46, 3491.32) * mm, v(32.9, 3491.11) * mm]});
            skFitSpline(sketch, "E245", {"points": [v(32.9, 3491.11) * mm, v(33.65, 3490.75) * mm, v(33.7, 3490.3) * mm, v(33.16, 3488.5) * mm]});
            skFitSpline(sketch, "E246", {"points": [v(33.16, 3488.5) * mm, v(31.16, 3481.86) * mm, v(27.73, 3477.33) * mm, v(23.57, 3475.84) * mm]});
            skFitSpline(sketch, "E247", {"points": [v(23.57, 3475.84) * mm, v(22.7, 3475.53) * mm, v(22.15, 3475.44) * mm, v(21.04, 3475.44) * mm]});
            skFitSpline(sketch, "E248", {"points": [v(21.04, 3475.44) * mm, v(18.8, 3475.43) * mm, v(17.63, 3475.98) * mm, v(16.46, 3477.57) * mm]});
            skFitSpline(sketch, "E249", {"points": [v(16.46, 3477.57) * mm, v(15.66, 3478.65) * mm, v(15.2, 3479.78) * mm, v(14.8, 3481.58) * mm]});
            skFitSpline(sketch, "E250", {"points": [v(14.13, 3482.13) * mm, v(13.35, 3480.81) * mm, v(11.83, 3479.04) * mm, v(11.03, 3478.53) * mm]});
            skFitSpline(sketch, "E251", {"points": [v(11.03, 3478.53) * mm, v(9.9, 3477.8) * mm, v(8.57, 3477.58) * mm, v(7.61, 3477.94) * mm]});
            skFitSpline(sketch, "E252", {"points": [v(7.61, 3477.94) * mm, v(6.27, 3478.45) * mm, v(5.4, 3479.84) * mm, v(4.98, 3482.13) * mm]});
            skFitSpline(sketch, "E253", {"points": [v(4.98, 3482.13) * mm, v(4.75, 3483.4) * mm, v(4.8, 3486.35) * mm, v(5.07, 3487.92) * mm]});
            skFitSpline(sketch, "E254", {"points": [v(5.07, 3487.92) * mm, v(5.2, 3488.68) * mm, v(5.29, 3489.33) * mm, v(5.26, 3489.36) * mm]});
            skFitSpline(sketch, "E255", {"points": [v(5.26, 3489.36) * mm, v(5.14, 3489.48) * mm, v(4.37, 3487.88) * mm, v(3.6, 3485.94) * mm]});
            skFitSpline(sketch, "E256", {"points": [v(3.6, 3485.94) * mm, v(2.27, 3482.6) * mm, v(1.23, 3479.2) * mm, v(1.06, 3477.67) * mm]});
            skFitSpline(sketch, "E257", {"points": [v(1.06, 3477.67) * mm, v(0.9, 3476.14) * mm, v(0.72, 3475.83) * mm, v(-0.26, 3475.33) * mm]});
            skFitSpline(sketch, "E258", {"points": [v(-0.26, 3475.33) * mm, v(-1.06, 3474.92) * mm, v(-2.51, 3474.93) * mm, v(-3.19, 3475.34) * mm]});
            skFitSpline(sketch, "E259", {"points": [v(22.53, 3491.28) * mm, v(23.3, 3491.85) * mm, v(23.52, 3492.5) * mm, v(23.44, 3494.08) * mm]});
            skFitSpline(sketch, "E260", {"points": [v(23.44, 3494.08) * mm, v(23.38, 3495.48) * mm, v(23.04, 3496.7) * mm, v(22.71, 3496.7) * mm]});
            skFitSpline(sketch, "E261", {"points": [v(22.71, 3496.7) * mm, v(22.12, 3496.7) * mm, v(21.2, 3494.52) * mm, v(20.42, 3491.25) * mm]});
            skFitSpline(sketch, "E262", {"points": [v(21.22, 3490.9) * mm, v(21.72, 3490.94) * mm, v(22.3, 3491.12) * mm, v(22.53, 3491.28) * mm]});
            skLineSegment(sketch, "E263.bottom", {"start": v(-7.33, 3378.8) * mm, "end": v(-1.5, 3378.8) * mm});
            skLineSegment(sketch, "E263.top", {"start": v(-7.33, 3438.65) * mm, "end": v(-1.5, 3438.65) * mm});
            skLineSegment(sketch, "E263.left", {"start": v(-7.33, 3378.8) * mm, "end": v(-7.33, 3438.65) * mm});
            skLineSegment(sketch, "E263.right", {"start": v(-1.5, 3378.8) * mm, "end": v(-1.5, 3438.65) * mm});
            skSolve(sketch);
        }
        {
            var Q0;
            {var subQ6=sQuery(id+"F0.wireOp",EDGE,"E196");Q0=makeQuery(id+"F0.imprint","IMPRINT",FACE,{"disambiguationData":[TD([[makeQuery(id+"F0.imprint","IMPRINT",EDGE,{"derivedFrom":subQ6}),-1.0]])]});}
            var Q1;
            Q1=makeQuery(id+"F0.imprint","IMPRINT",FACE,{"disambiguationData":[TD([[makeQuery(id+"F0.imprint","IMPRINT",EDGE,{"derivedFrom":sQuery(id+"F0.wireOp",EDGE,"E0")}),-1.0]])]});
            var Q2;
            Q2=makeQuery(id+"F0.imprint","IMPRINT",FACE,{"disambiguationData":[TD([[makeQuery(id+"F0.imprint","IMPRINT",EDGE,{"derivedFrom":sQuery(id+"F0.wireOp",EDGE,"E30")}),-1.0]])]});
            var Q3;
            Q3=makeQuery(id+"F0.imprint","IMPRINT",FACE,{"disambiguationData":[TD([[makeQuery(id+"F0.imprint","IMPRINT",EDGE,{"derivedFrom":sQuery(id+"F0.wireOp",EDGE,"E6")}),-1.0]])]});
            var Q4;
            {var subQ0=sQuery(id+"F0.wireOp",EDGE,"E263.bottom");Q4=makeQuery(id+"F0.imprint","IMPRINT",FACE,{"disambiguationData":[TD([[makeQuery(id+"F0.imprint","IMPRINT",EDGE,{"derivedFrom":subQ0}),1.0]])]});}
            var Q5;
            {var subQ0=sQuery(id+"F0.wireOp",EDGE,"E263.right");var subQ1=sQuery(id+"F0.wireOp",EDGE,"E82");var subQ2=makeQuery(id+"F0.imprint","INTERSECT",VERTEX,{"derivedFrom":[subQ1,subQ0]});Q5=makeQuery(id+"F0.imprint","IMPRINT",FACE,{"disambiguationData":[TD([[makeQuery(id+"F0.imprint","IMPRINT",EDGE,{"disambiguationData":[TD([[subQ2,-1.0]])],"derivedFrom":subQ1}),-1.0]])]});}
            var Q6;
            {var subQ0=sQuery(id+"F0.wireOp",EDGE,"E80");var subQ1=sQuery(id+"F0.wireOp",EDGE,"E79");var subQ2=makeQuery(id+"F0.imprint","INTERSECT",VERTEX,{"derivedFrom":[subQ1,subQ0]});Q6=makeQuery(id+"F0.imprint","IMPRINT",FACE,{"disambiguationData":[TD([[makeQuery(id+"F0.imprint","IMPRINT",EDGE,{"disambiguationData":[TD([[subQ2,1.0]])],"derivedFrom":subQ1}),-1.0]])]});}
            var Q7;
            {var subQ5=sQuery(id+"F0.wireOp",EDGE,"E218");Q7=makeQuery(id+"F0.imprint","IMPRINT",FACE,{"disambiguationData":[TD([[makeQuery(id+"F0.imprint","IMPRINT",EDGE,{"derivedFrom":subQ5}),-1.0]])]});}
            var Q8;
            {var subQ0=sQuery(id+"F0.wireOp",EDGE,"E76");var subQ1=sQuery(id+"F0.wireOp",EDGE,"E75");var subQ2=makeQuery(id+"F0.imprint","INTERSECT",VERTEX,{"derivedFrom":[subQ1,subQ0]});Q8=makeQuery(id+"F0.imprint","IMPRINT",FACE,{"disambiguationData":[TD([[makeQuery(id+"F0.imprint","IMPRINT",EDGE,{"disambiguationData":[TD([[subQ2,1.0]])],"derivedFrom":subQ1}),-1.0]])]});}
            extrude(context, id + "F1", {"entities" : qUnion([Q0, Q1, Q2, Q3, Q4, Q5, Q6, Q7, Q8]), "depth" : 1.52 * mm, "offsetDistance" : 25.4 * mm});
        }
    });
